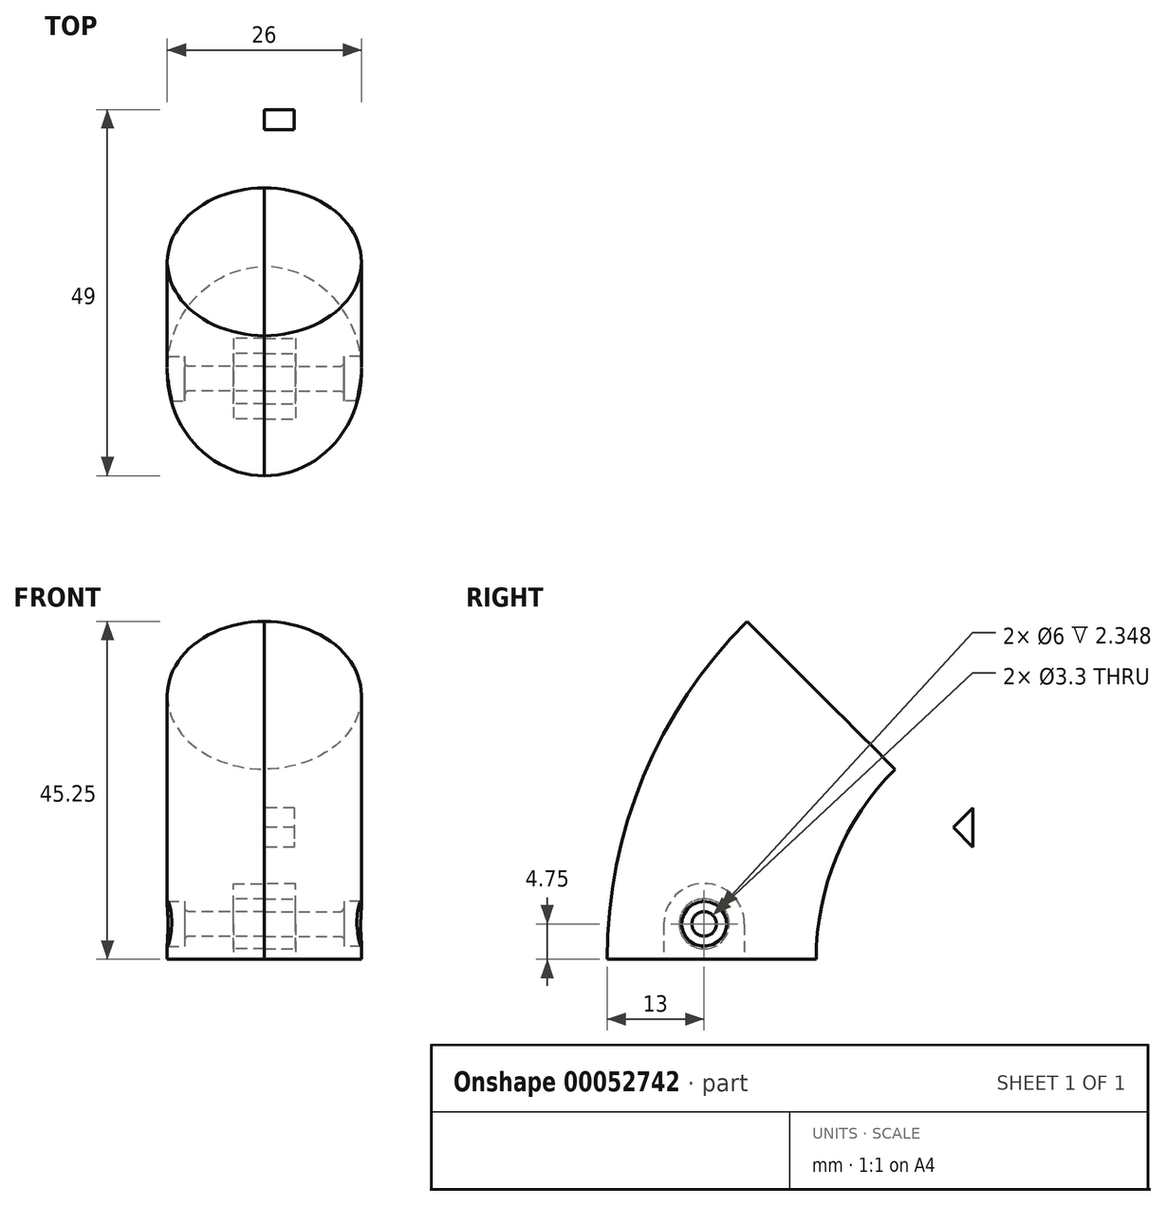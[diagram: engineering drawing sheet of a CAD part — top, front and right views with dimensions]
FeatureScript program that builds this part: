
annotation { "Feature Type Name" : "Feature", "Feature Type Description" : "" }
export const myFeature = defineFeature(function(context is Context, id is Id, definition is map)
    precondition{}
    {
        {
            var Q0;
            Q0=qCreatedBy(makeId("Top.planeOp"),FACE);
            var sketch = newSketch(context, id + "F0", { "sketchPlane" : qUnion([Q0])});
            skEllipse(sketch, "E0", {"center": v(0, 0) * mm, "majorRadius": 14 * mm, "minorRadius": 13 * mm, "majorAxis": v(0, 1)});
            skLineSegment(sketch, "E1", {"start": v(0, 0) * mm, "end": v(0, 50) * mm, "construction": true});
            skLineSegment(sketch, "E2", {"start": v(0, 50) * mm, "end": v(27.53, 50) * mm, "construction": true});
            skLineSegment(sketch, "E3.rect.bottom", {"start": v(-4.15, 4.4) * mm, "end": v(4.15, 4.4) * mm});
            skLineSegment(sketch, "E3.rect.top", {"start": v(-4.15, -6.4) * mm, "end": v(4.15, -6.4) * mm});
            skLineSegment(sketch, "E3.rect.left", {"start": v(-4.15, 4.4) * mm, "end": v(-4.15, -6.4) * mm});
            skLineSegment(sketch, "E3.rect.right", {"start": v(4.15, 4.4) * mm, "end": v(4.15, -6.4) * mm});
            skLineSegment(sketch, "E4", {"start": v(0, 0) * mm, "end": v(0, -6.4) * mm, "construction": true});
            skLineSegment(sketch, "E5", {"start": v(0, 0) * mm, "end": v(4.15, 0) * mm, "construction": true});
            skSolve(sketch);
        }
        {
            var Q0;
            Q0=makeQuery(id+"F0.imprint","IMPRINT",FACE,{"disambiguationData":[TD([[makeQuery(id+"F0.imprint","IMPRINT",EDGE,{"derivedFrom":sQuery(id+"F0.wireOp",EDGE,"E0")}),1.0]])]});
            var Q1;
            Q1=makeQuery(id+"F0.imprint","IMPRINT",FACE,{"disambiguationData":[TD([[makeQuery(id+"F0.imprint","IMPRINT",EDGE,{"derivedFrom":sQuery(id+"F0.wireOp",EDGE,"E3.rect.bottom")}),-1.0]])]});
            var Q2;
            Q2=sQuery(id+"F0.wireOp",EDGE,"E2");
            revolve(context, id + "F1", {"entities" : qUnion([Q0, Q1]), "axis" : qUnion([Q2]), "revolveType" : RevolveType.ONE_DIRECTION, "oppositeDirection" : true, "angle" : 45 * degree});
        }
        {
            var Q0;
            Q0=makeQuery(id+"F1.opRevolve","CAP_FACE",FACE,{"disambiguationData":[OSD([sQuery(id+"F0.wireOp",EDGE,"E0")])],"isStart":false});
            var sketch = newSketch(context, id + "F2", { "sketchPlane" : qUnion([Q0])});
            skLineSegment(sketch, "E6.rect.bottom", {"start": v(-4, -10.4) * mm, "end": v(4, -10.4) * mm});
            skLineSegment(sketch, "E6.rect.top", {"start": v(-4, -20.9) * mm, "end": v(4, -20.9) * mm});
            skLineSegment(sketch, "E6.rect.left", {"start": v(-4, -10.4) * mm, "end": v(-4, -20.9) * mm});
            skLineSegment(sketch, "E6.rect.right", {"start": v(4, -10.4) * mm, "end": v(4, -20.9) * mm});
            skPoint(sketch, "E7.orphan", {"position": v(0, -28.64) * mm});
            skLineSegment(sketch, "E8", {"start": v(0, -0.64) * mm, "end": v(0, -10.4) * mm});
            skLineSegment(sketch, "E9", {"start": v(0, -10.4) * mm, "end": v(0, -14.64) * mm});
            skSolve(sketch);
        }
        {
            var Q0;
            Q0=makeQuery(id+"F2.imprint","IMPRINT",FACE,{"disambiguationData":[TD([[makeQuery(id+"F2.imprint","IMPRINT",EDGE,{"derivedFrom":sQuery(id+"F2.wireOp",EDGE,"E6.rect.bottom")}),-1.0]])]});
            extrude(context, id + "F3", {"entities" : qUnion([Q0]), "operationType" : NewBodyOperationType.ADD, "depth" : 10 * mm});
        }
        {
            var Q0;
            Q0=makeQuery(id+"F3.opExtrude","CAP_EDGE",EDGE,{"disambiguationData":[OSD([sQuery(id+"F2.wireOp",EDGE,"E6.rect.top")])],"isStart":false});
            var Q1;
            Q1=makeQuery(id+"F3.opExtrude","CAP_EDGE",EDGE,{"disambiguationData":[OSD([sQuery(id+"F2.wireOp",EDGE,"E6.rect.bottom")])],"isStart":false});
            fillet(context, id + "F4", {"entities" : qUnion([Q0, Q1]), "radius" : 5.25 * mm, "tangentPropagation" : true, "allowEdgeOverflow" : false});
        }
        {
            var Q0;
            Q0=makeQuery(id+"F3.opExtrude","SWEPT_FACE",FACE,{"disambiguationData":[OSD([sQuery(id+"F2.wireOp",EDGE,"E6.rect.right")])]});
            var sketch = newSketch(context, id + "F5", { "sketchPlane" : qUnion([Q0])});
            skLineSegment(sketch, "E10", {"start": v(13.94, 36.06) * mm, "end": v(17.3, 39.42) * mm, "construction": true});
            skCircle(sketch, "E11", {"center": v(17.3, 39.42) * mm, "radius": 3.5 * mm});
            skSolve(sketch);
        }
        {
            var Q0;
            Q0=qSketchRegion(id+"F5",true);
            extrude(context, id + "F6", {"entities" : qUnion([Q0]), "operationType" : NewBodyOperationType.REMOVE, "endBound" : BoundingType.THROUGH_ALL, "oppositeDirection" : true, "depth" : 25 * mm});
        }
        {
            var Q0;
            Q0=makeQuery(id+"F0.imprint","IMPRINT",FACE,{"disambiguationData":[TD([[makeQuery(id+"F0.imprint","IMPRINT",EDGE,{"derivedFrom":sQuery(id+"F0.wireOp",EDGE,"E3.rect.bottom")}),-1.0]])]});
            extrude(context, id + "F7", {"entities" : qUnion([Q0]), "operationType" : NewBodyOperationType.REMOVE, "depth" : 10.15 * mm});
        }
        {
            var Q0;
            Q0=makeQuery(id+"F7.boolean.opBoolean","COPY",EDGE,{"derivedFrom":makeQuery(id+"F7.opExtrude","CAP_EDGE",EDGE,{"disambiguationData":[OSD([sQuery(id+"F0.wireOp",EDGE,"E3.rect.bottom")])],"isStart":false})});
            var Q1;
            Q1=makeQuery(id+"F7.boolean.opBoolean","COPY",EDGE,{"derivedFrom":makeQuery(id+"F7.opExtrude","CAP_EDGE",EDGE,{"disambiguationData":[OSD([sQuery(id+"F0.wireOp",EDGE,"E3.rect.top")])],"isStart":false})});
            fillet(context, id + "F8", {"entities" : qUnion([Q0, Q1]), "radius" : 5.4 * mm, "tangentPropagation" : true, "allowEdgeOverflow" : false});
        }
        {
            var Q0;
            Q0=qCreatedBy(makeId("Top.planeOp"),FACE);
            var sketch = newSketch(context, id + "F9", { "sketchPlane" : qUnion([Q0])});
            skLineSegment(sketch, "E12.bottom", {"start": v(0, 35) * mm, "end": v(20, 35) * mm});
            skLineSegment(sketch, "E12.top", {"start": v(0, -35) * mm, "end": v(20, -35) * mm});
            skLineSegment(sketch, "E12.left", {"start": v(0, 35) * mm, "end": v(0, -35) * mm});
            skLineSegment(sketch, "E12.right", {"start": v(20, 35) * mm, "end": v(20, -35) * mm});
            skLineSegment(sketch, "E13", {"start": v(20, 35) * mm, "end": v(20, 0) * mm, "construction": true});
            skSolve(sketch);
        }
        {
            var Q0;
            Q0=qSketchRegion(id+"F9",true);
            extrude(context, id + "F10", {"entities" : qUnion([Q0]), "operationType" : NewBodyOperationType.INTERSECT, "depth" : 50 * mm});
        }
        {
            var Q0;
            Q0=makeQuery(id+"F7.boolean.opBoolean","COPY",FACE,{"derivedFrom":makeQuery(id+"F7.opExtrude","SWEPT_FACE",FACE,{"disambiguationData":[OSD([sQuery(id+"F0.wireOp",EDGE,"E3.rect.right")])]})});
            var sketch = newSketch(context, id + "F11", { "sketchPlane" : qUnion([Q0])});
            skCircle(sketch, "E14", {"center": v(1, 4.75) * mm, "radius": 3.35 * mm});
            skCircle(sketch, "E15", {"center": v(1, 4.75) * mm, "radius": 1.65 * mm});
            skSolve(sketch);
        }
        {
            var Q0;
            Q0=makeQuery(id+"F11.imprint","IMPRINT",FACE,{"disambiguationData":[TD([[makeQuery(id+"F11.imprint","IMPRINT",EDGE,{"derivedFrom":sQuery(id+"F11.wireOp",EDGE,"E14")}),1.0]])]});
            var Q1;
            Q1=makeQuery(id+"F1.opRevolve","SWEPT_BODY",BODY,{"disambiguationData":[OSD([sQuery(id+"F0.wireOp",EDGE,"E0")])]});
            extrude(context, id + "F12", {"entities" : qUnion([Q0]), "operationType" : NewBodyOperationType.ADD, "endBoundEntityBody" : qUnion([Q1]), "depth" : 4.15 * mm});
        }
        {
            var Q0;
            Q0=makeQuery(id+"F12.boolean.opBoolean","SPLIT",FACE,{"disambiguationData":[TD([makeQuery(id+"F12.opExtrude","SWEPT_FACE",FACE,{"disambiguationData":[OSD([sQuery(id+"F11.wireOp",EDGE,"E15")])]})])],"derivedFrom":makeQuery(id+"F7.boolean.opBoolean","COPY",FACE,{"derivedFrom":makeQuery(id+"F7.opExtrude","SWEPT_FACE",FACE,{"disambiguationData":[OSD([sQuery(id+"F0.wireOp",EDGE,"E3.rect.right")])]})})});
            extrude(context, id + "F13", {"entities" : qUnion([Q0]), "operationType" : NewBodyOperationType.REMOVE, "oppositeDirection" : true, "depth" : 25 * mm});
        }
        {
            var Q0;
            Q0=makeQuery(id+"F12.boolean.opBoolean","SPLIT",FACE,{"disambiguationData":[TD([makeQuery(id+"F1.opRevolve","CAP_FACE",FACE,{"disambiguationData":[OSD([sQuery(id+"F0.wireOp",EDGE,"E0")])],"isStart":true})])],"derivedFrom":makeQuery(id+"F7.boolean.opBoolean","COPY",FACE,{"derivedFrom":makeQuery(id+"F7.opExtrude","SWEPT_FACE",FACE,{"disambiguationData":[OSD([sQuery(id+"F0.wireOp",EDGE,"E3.rect.right")])]})})});
            var sketch = newSketch(context, id + "F14", { "sketchPlane" : qUnion([Q0])});
            skPoint(sketch, "E16.0.midPoint", {"position": v(1, 7.6) * mm});
            skCircle(sketch, "E17", {"center": v(1, 4.75) * mm, "radius": 1.65 * mm});
            skCircle(sketch, "E18", {"center": v(1, 4.75) * mm, "radius": 3 * mm});
            skSolve(sketch);
        }
        {
            var Q0;
            Q0=qSketchRegion(id+"F14",true);
            extrude(context, id + "F15", {"entities" : qUnion([Q0]), "operationType" : NewBodyOperationType.REMOVE, "oppositeDirection" : true, "depth" : 25 * mm});
        }
        {
            var Q0;
            Q0=qSketchRegion(id+"F14",true);
            extrude(context, id + "F16", {"entities" : qUnion([Q0]), "operationType" : NewBodyOperationType.ADD, "oppositeDirection" : true, "depth" : 6.5 * mm});
        }
        {
            var Q0;
            Q0=makeQuery(id+"F15.boolean.opBoolean","INTERSECT",EDGE,{"derivedFrom":[makeQuery(id+"F1.opRevolve","SWEPT_FACE",FACE,{"disambiguationData":[OSD([sQuery(id+"F0.wireOp",EDGE,"E0")])]}),makeQuery(id+"F15.opExtrude","SWEPT_FACE",FACE,{"disambiguationData":[OSD([sQuery(id+"F14.wireOp",EDGE,"E16.3")])]})]});
            var Q1;
            Q1=makeQuery(id+"F15.boolean.opBoolean","INTERSECT",EDGE,{"derivedFrom":[makeQuery(id+"F1.opRevolve","SWEPT_FACE",FACE,{"disambiguationData":[OSD([sQuery(id+"F0.wireOp",EDGE,"E0")])]}),makeQuery(id+"F15.opExtrude","SWEPT_FACE",FACE,{"disambiguationData":[OSD([sQuery(id+"F14.wireOp",EDGE,"E16.2")])]})]});
            var Q2;
            Q2=makeQuery(id+"F15.boolean.opBoolean","INTERSECT",EDGE,{"derivedFrom":[makeQuery(id+"F1.opRevolve","SWEPT_FACE",FACE,{"disambiguationData":[OSD([sQuery(id+"F0.wireOp",EDGE,"E0")])]}),makeQuery(id+"F15.opExtrude","SWEPT_FACE",FACE,{"disambiguationData":[OSD([sQuery(id+"F14.wireOp",EDGE,"E16.1")])]})]});
            var Q3;
            Q3=makeQuery(id+"F15.boolean.opBoolean","INTERSECT",EDGE,{"derivedFrom":[makeQuery(id+"F1.opRevolve","SWEPT_FACE",FACE,{"disambiguationData":[OSD([sQuery(id+"F0.wireOp",EDGE,"E0")])]}),makeQuery(id+"F15.opExtrude","SWEPT_FACE",FACE,{"disambiguationData":[OSD([sQuery(id+"F14.wireOp",EDGE,"E16.0")])]})]});
            var Q4;
            Q4=makeQuery(id+"F15.boolean.opBoolean","INTERSECT",EDGE,{"derivedFrom":[makeQuery(id+"F1.opRevolve","SWEPT_FACE",FACE,{"disambiguationData":[OSD([sQuery(id+"F0.wireOp",EDGE,"E0")])]}),makeQuery(id+"F15.opExtrude","SWEPT_FACE",FACE,{"disambiguationData":[OSD([sQuery(id+"F14.wireOp",EDGE,"E16.5")])]})]});
            var Q5;
            Q5=makeQuery(id+"F15.boolean.opBoolean","INTERSECT",EDGE,{"derivedFrom":[makeQuery(id+"F1.opRevolve","SWEPT_FACE",FACE,{"disambiguationData":[OSD([sQuery(id+"F0.wireOp",EDGE,"E0")])]}),makeQuery(id+"F15.opExtrude","SWEPT_FACE",FACE,{"disambiguationData":[OSD([sQuery(id+"F14.wireOp",EDGE,"E16.4")])]})]});
            var Q6;
            Q6=makeQuery(id+"F16.opExtrude","CAP_EDGE",EDGE,{"disambiguationData":[OSD([sQuery(id+"F14.wireOp",EDGE,"E17")])],"isStart":false});
            fillet(context, id + "F17", {"entities" : qUnion([Q0, Q1, Q2, Q3, Q4, Q5, Q6]), "radius" : 0.5 * mm, "tangentPropagation" : true, "allowEdgeOverflow" : false});
        }
        {
            var Q0;
            Q0=makeQuery(id+"F1.opRevolve","SWEPT_BODY",BODY,{"disambiguationData":[OSD([sQuery(id+"F0.wireOp",EDGE,"E0")])]});
            var Q1;
            Q1=qCreatedBy(makeId("Right.planeOp"),FACE);
            mirror(context, id + "F18", {"entities" : qUnion([Q0]), "mirrorPlane" : qUnion([Q1])});
        }
    });
